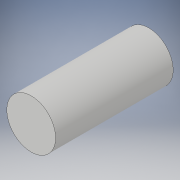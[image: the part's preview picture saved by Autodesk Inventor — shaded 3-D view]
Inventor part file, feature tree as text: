
AUTODESK INVENTOR PART (.ipt)
format: ipt  version: 2019.4 (Build 234330000, 330)  size: 92,672 bytes
history: native  units: mm
features: other x1, extrude x1, sketch x1
ambient origin geometry x8: Origin, YZ Plane, XZ Plane, XY Plane, X Axis, Y Axis, Z Axis, Center Point
bodies: Body1 (feature_tree)
feature tree (3):
  other  "Sólido1"
  extrude  "Extrusión1"  Depth=600.0mm TaperAngle=0.0deg
  sketch  "Boceto1"  dims[d0=249.0mm d1=600.0mm d2=0.0mm]
